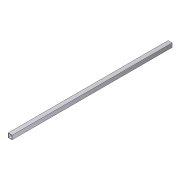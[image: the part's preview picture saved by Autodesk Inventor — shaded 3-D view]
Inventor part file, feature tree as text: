
AUTODESK INVENTOR PART (.ipt)
format: ipt  version: 2012 (Build 160160000, 160)  size: 72,704 bytes
history: native  units: in
note: dims shown in document units (in); Inventor stores cm internally (conversion verified against a paired STEP export)
features: extrude x1, sketch x1
ambient origin geometry x8: Origin, YZ Plane, XZ Plane, XY Plane, X Axis, Y Axis, Z Axis, Center Point
bodies: Solid1 (feature_tree)
feature tree (2):
  extrude  "Extrusion1"  Depth=1.75in
  sketch  "Sketch1"  dims[d0=1.75in d1=1.75in d2=0.125in d3=0.125in d4=0.125in d5=0.125in d6=70.0in d7=0.0in]
